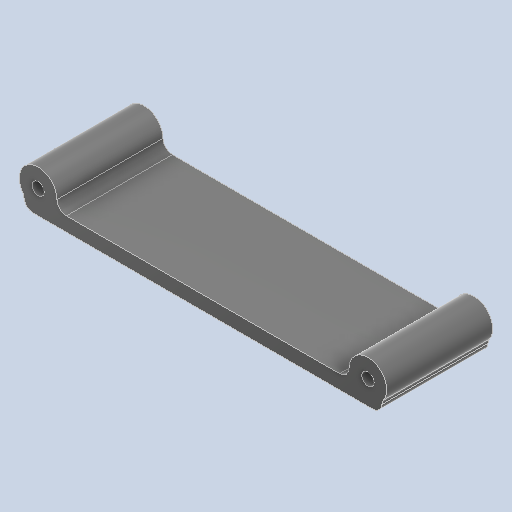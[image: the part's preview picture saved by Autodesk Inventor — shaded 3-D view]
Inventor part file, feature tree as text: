
AUTODESK INVENTOR PART (.ipt)
format: ipt  version: 2025.1 (Build 291241000, 241)  size: 256,000 bytes
history: native  units: mm
features: other x7, fillet x4, reference x3, sketch x2, extrude x2, projected_geometry x1
ambient origin geometry x8: Origin, YZ Plane, XZ Plane, XY Plane, X Axis, Y Axis, Z Axis, Center Point
bodies: Body1 (feature_tree)
feature tree (19):
  other  "ソリッド1"
  sketch  "スケッチ1"
  other  "作業平面1"
  other  "作業平面2"
  other  "作業平面3"
  extrude  "押し出し1"  Depth=2.6mm
  fillet  "フィレット1"  Radius=8.0mm
  extrude  "押し出し2"  Depth=2.6mm
  fillet  "フィレット2"  Radius=8.0mm
  fillet  "フィレット3"  Radius=3.0mm
  fillet  "フィレット4"  Radius=10.0mm
  reference  "参照1"
  reference  "参照2"
  reference  "参照3"
  sketch  "スケッチ2"
  projected_geometry  "投影ループ1"
  other  "<userpath>\Documents\Inventor\Vixen\doutai.iam"
  other  "doutai.iam"
  other  "badcase:1"
